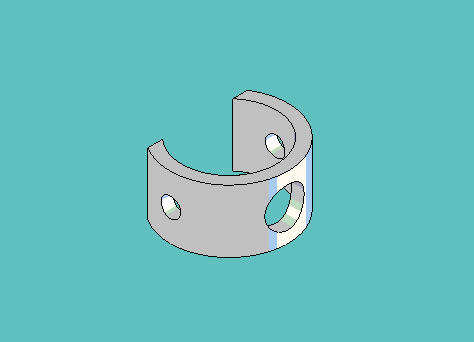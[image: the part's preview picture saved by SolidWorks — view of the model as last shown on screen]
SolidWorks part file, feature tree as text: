
SOLIDWORKS PART (.sldprt)
format: sldprt  version: not decoded by parser v0  size: 348,672 bytes
history: native  units: mm
features: sketch x4, cut_extrude x2, material x1, extrude x1 (+11 scaffold rows collapsed)
feature tree (19):
  scaffold x11  (default folders/planes/origin — collapsed)
  material  "Material <not specified>"
  sketch  "Sketch1"  dims[D1=19.05mm D2=~2.38125mm D3=6.35mm]
  extrude  "Extrude1"  Depth=12.7mm
  sketch  "Sketch2"  dims[D1=7.9375mm D2=~2.38125mm D3=~2.38125mm D4=12.7mm]
  cut_extrude  "Cut-Extrude1"  [1 undecoded]
  sketch  "Sketch3"  dims[D1=~3.96875mm]
  cut_extrude  "Cut-Extrude2"  [1 undecoded]
  sketch  "Sketch4"  dims[c1.D3=9.525mm c1.D5=9.525mm c1.D2=17.4625mm c2.D3=1.5875mm c2.D4=~18.25625mm c2.D5=~2.38125mm c2.D6=11.1125mm c2.D7=~11.90625mm c2.D1=0.0mm]
decode coverage: 5 of 7 modeling features carry decoded parameters
note: ~ marks probable driven/reference dimensions
note: 2 parameter values undecoded
note: suppression state not decoded; provenance and decode notes live in map.json
